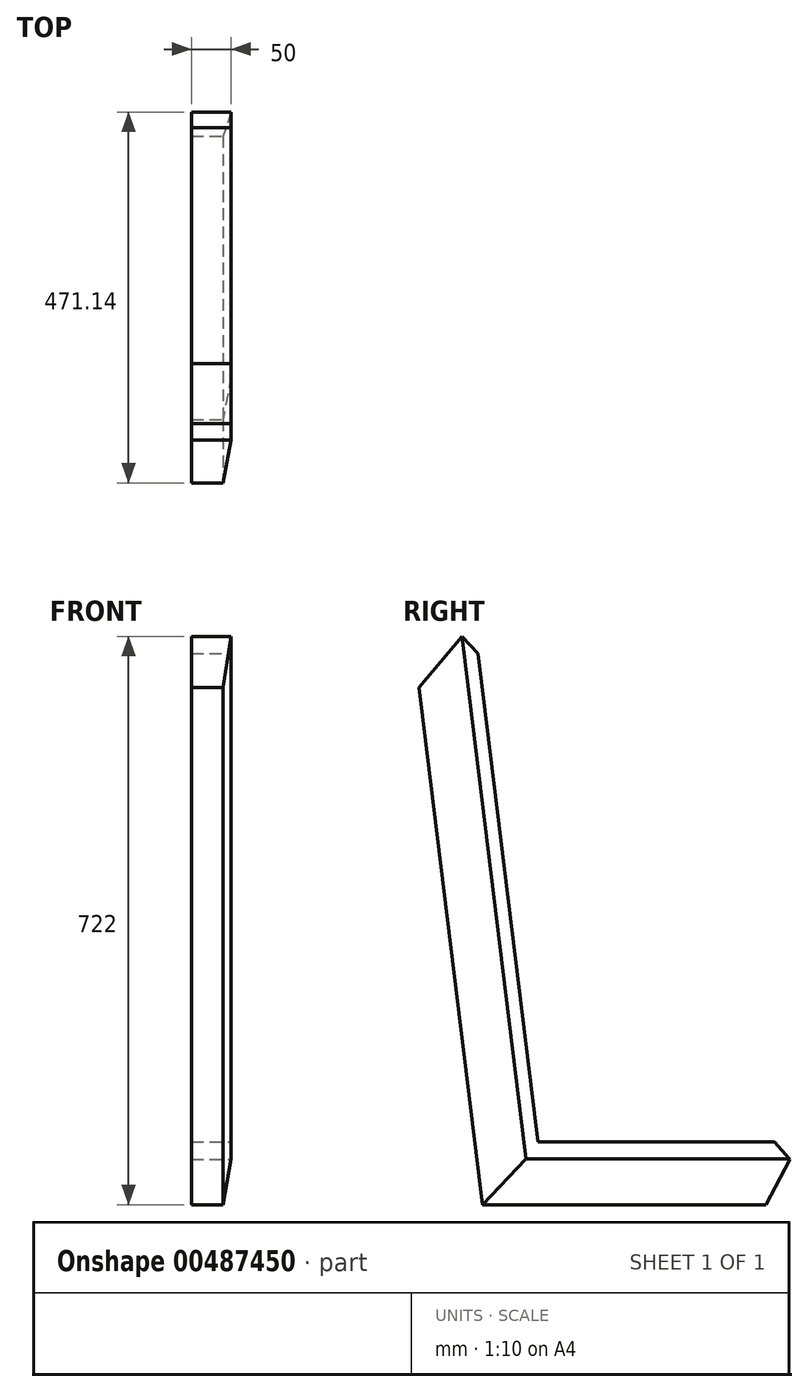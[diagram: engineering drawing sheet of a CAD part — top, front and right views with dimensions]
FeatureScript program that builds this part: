
annotation { "Feature Type Name" : "Feature", "Feature Type Description" : "" }
export const myFeature = defineFeature(function(context is Context, id is Id, definition is map)
    precondition{}
    {
        {
            var Q0;
            Q0=qCreatedBy(makeId("Right.planeOp"),FACE);
            var sketch = newSketch(context, id + "F0", { "sketchPlane" : qUnion([Q0])});
            skLineSegment(sketch, "E0.bottom", {"start": v(0, 0) * mm, "end": v(482.8, 0) * mm, "construction": true});
            skLineSegment(sketch, "E0.top", {"start": v(0, 1100) * mm, "end": v(482.8, 1100) * mm, "construction": true});
            skLineSegment(sketch, "E0.left", {"start": v(0, 0) * mm, "end": v(0, 1100) * mm, "construction": true});
            skLineSegment(sketch, "E0.right", {"start": v(482.8, 0) * mm, "end": v(482.8, 1100) * mm, "construction": true});
            skLineSegment(sketch, "E1", {"start": v(463.07, 400) * mm, "end": v(482.8, 377.4) * mm});
            skLineSegment(sketch, "E2", {"start": v(482.8, 377.4) * mm, "end": v(452.29, 320) * mm});
            skLineSegment(sketch, "E3", {"start": v(452.29, 320) * mm, "end": v(92.29, 320) * mm});
            skLineSegment(sketch, "E4", {"start": v(163.07, 400) * mm, "end": v(463.07, 400) * mm});
            skLineSegment(sketch, "E5", {"start": v(11.65, 976.76) * mm, "end": v(92.29, 320) * mm});
            skLineSegment(sketch, "E6", {"start": v(163.07, 400) * mm, "end": v(86.9, 1020.34) * mm});
            skLineSegment(sketch, "E7", {"start": v(86.9, 1020.34) * mm, "end": v(66.14, 1042) * mm});
            skLineSegment(sketch, "E8", {"start": v(66.14, 1042) * mm, "end": v(11.65, 976.76) * mm});
            skSolve(sketch);
        }
        {
            var Q0;
            Q0=qSketchRegion(id+"F0",true);
            extrude(context, id + "F1", {"entities" : qUnion([Q0]), "oppositeDirection" : true, "depth" : 50 * mm});
        }
        {
            var Q0;
            Q0=makeQuery(id+"F1.opExtrude","CAP_EDGE",EDGE,{"disambiguationData":[OSD([sQuery(id+"F0.wireOp",EDGE,"E5")])],"isStart":true});
            chamfer(context, id + "F2", {"entities" : qUnion([Q0]), "chamferType" : ChamferType.TWO_OFFSETS, "width1" : 62 * mm, "oppositeDirection" : false, "width2" : 10 * mm, "tangentPropagation" : true});
        }
        {
            var Q0;
            Q0=makeQuery(id+"F1.opExtrude","CAP_EDGE",EDGE,{"disambiguationData":[OSD([sQuery(id+"F0.wireOp",EDGE,"E3")])],"isStart":true});
            chamfer(context, id + "F3", {"entities" : qUnion([Q0]), "chamferType" : ChamferType.TWO_OFFSETS, "width1" : 10 * mm, "oppositeDirection" : false, "width2" : 58 * mm, "tangentPropagation" : true});
        }
    });
